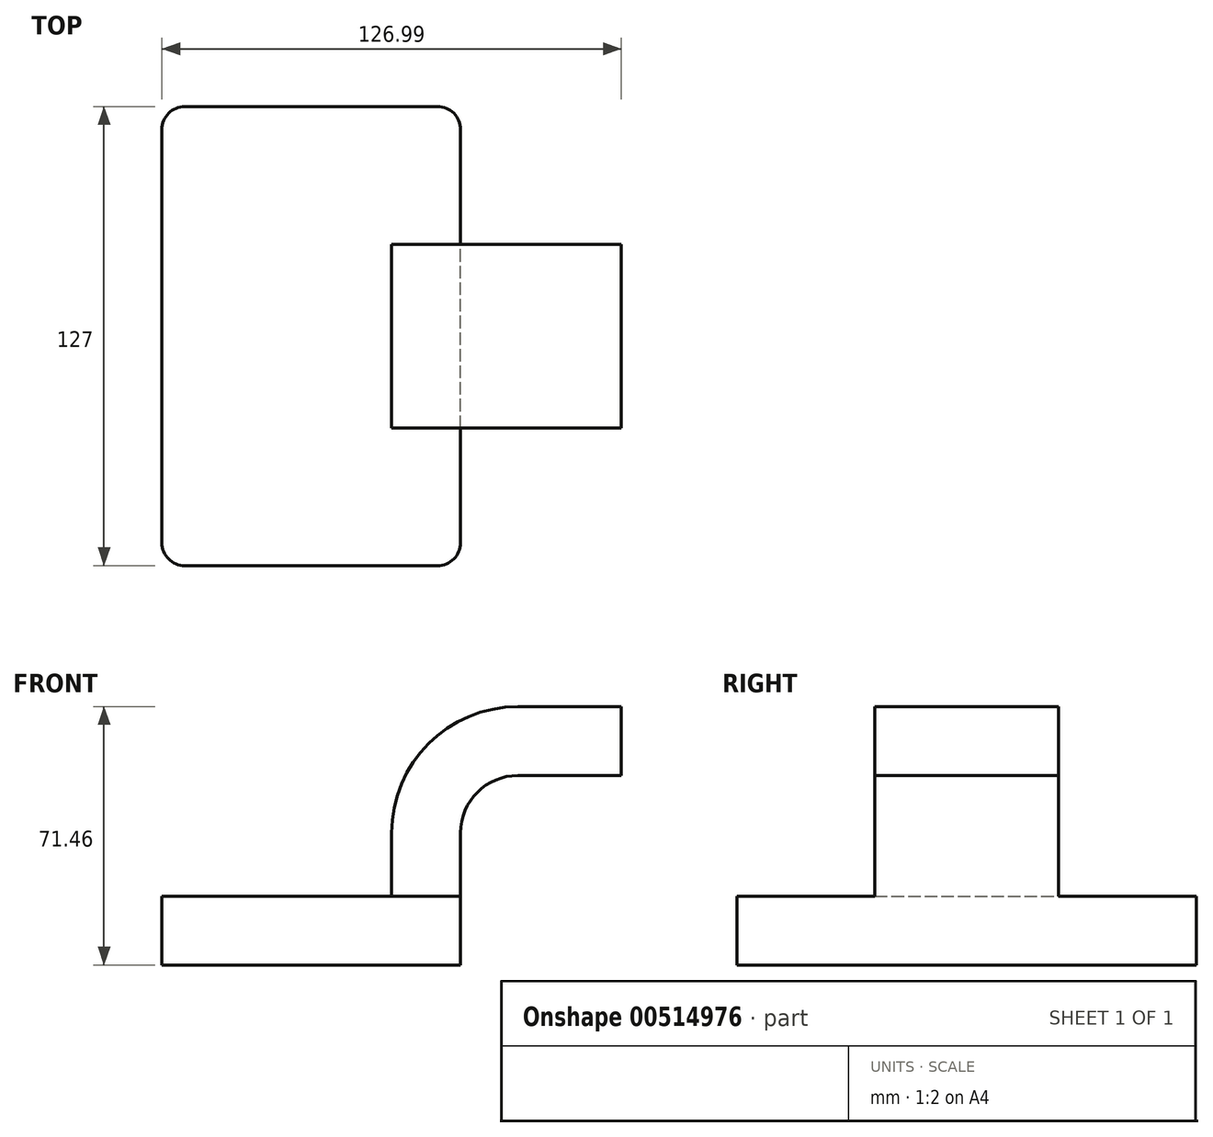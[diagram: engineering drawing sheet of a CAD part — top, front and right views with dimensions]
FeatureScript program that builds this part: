
annotation { "Feature Type Name" : "Feature", "Feature Type Description" : "" }
export const myFeature = defineFeature(function(context is Context, id is Id, definition is map)
    precondition{}
    {
        {
            var Q0;
            Q0=qCreatedBy(makeId("Front.planeOp"),FACE);
            var sketch = newSketch(context, id + "F0", { "sketchPlane" : qUnion([Q0])});
            skLineSegment(sketch, "E0.bottom", {"start": v(41.27, 9.53) * mm, "end": v(-41.28, 9.53) * mm});
            skLineSegment(sketch, "E0.top", {"start": v(41.28, -9.52) * mm, "end": v(-41.27, -9.53) * mm});
            skLineSegment(sketch, "E0.left", {"start": v(41.28, 9.53) * mm, "end": v(41.28, -9.52) * mm});
            skLineSegment(sketch, "E0.right", {"start": v(-41.28, 9.53) * mm, "end": v(-41.27, -9.53) * mm});
            skPoint(sketch, "E0.middle", {"position": v(0, 0) * mm});
            skLineSegment(sketch, "E1.bottom", {"start": v(111.13, 38.1) * mm, "end": v(60.33, 38.1) * mm});
            skLineSegment(sketch, "E1.top", {"start": v(111.13, 66.68) * mm, "end": v(60.33, 66.68) * mm});
            skLineSegment(sketch, "E1.left", {"start": v(111.13, 38.1) * mm, "end": v(111.13, 66.68) * mm});
            skLineSegment(sketch, "E1.right", {"start": v(60.33, 38.1) * mm, "end": v(60.33, 66.68) * mm});
            skPoint(sketch, "E1.middle", {"position": v(85.73, 52.39) * mm});
            skLineSegment(sketch, "E2", {"start": v(41.27, 9.53) * mm, "end": v(41.27, 27) * mm});
            skArc(sketch, "E3", {"start": v(41.28, 27) * mm, "mid": v(45.92, 38.23) * mm, "end": v(57.15, 42.88) * mm});
            skLineSegment(sketch, "E4", {"start": v(57.15, 42.88) * mm, "end": v(85.73, 42.88) * mm});
            skArc(sketch, "E5.0", {"start": v(22.23, 27) * mm, "mid": v(32.45, 51.7) * mm, "end": v(57.15, 61.93) * mm});
            skLineSegment(sketch, "E6", {"start": v(85.73, 42.88) * mm, "end": v(85.73, 61.93) * mm});
            skLineSegment(sketch, "E7", {"start": v(57.15, 61.93) * mm, "end": v(85.73, 61.93) * mm});
            skLineSegment(sketch, "E8", {"start": v(22.23, 27) * mm, "end": v(22.23, 9.53) * mm});
            skFitSpline(sketch, "E9", {"points": [v(-41.28, 9.53) * mm, v(57.15, 61.93) * mm], "startDerivative": vector(-16.87, 98.83) * mm, "endDerivative": vector(148.65, -3.4) * mm});
            skSolve(sketch);
        }
        {
            var Q0;
            Q0=makeQuery(id+"F0.imprint","IMPRINT",FACE,{"disambiguationData":[TD([[makeQuery(id+"F0.imprint","IMPRINT",EDGE,{"derivedFrom":sQuery(id+"F0.wireOp",EDGE,"E0.top")}),-1.0]])]});
            extrude(context, id + "F1", {"entities" : qUnion([Q0]), "endBound" : BoundingType.SYMMETRIC, "depth" : 127 * mm});
        }
        {
            var Q0;
            {var subQ1=sQuery(id+"F0.wireOp",EDGE,"E2");Q0=makeQuery(id+"F0.imprint","IMPRINT",FACE,{"disambiguationData":[TD([[makeQuery(id+"F0.imprint","IMPRINT",EDGE,{"derivedFrom":subQ1}),1.0]])]});}
            var Q1;
            {var subQ5=sQuery(id+"F0.wireOp",EDGE,"E6");Q1=makeQuery(id+"F0.imprint","IMPRINT",FACE,{"disambiguationData":[TD([[makeQuery(id+"F0.imprint","IMPRINT",EDGE,{"derivedFrom":subQ5}),1.0]])]});}
            extrude(context, id + "F2", {"entities" : qUnion([Q0, Q1]), "operationType" : NewBodyOperationType.ADD, "endBound" : BoundingType.SYMMETRIC, "depth" : 50.8 * mm});
        }
        {
            var Q0;
            Q0=makeQuery(id+"F0.imprint","IMPRINT",FACE,{"disambiguationData":[TD([[makeQuery(id+"F0.imprint","IMPRINT",EDGE,{"derivedFrom":sQuery(id+"F0.wireOp",EDGE,"E5.0")}),1.0]])]});
            extrude(context, id + "F3", {"entities" : qUnion([Q0]), "operationType" : NewBodyOperationType.ADD, "endBound" : BoundingType.SYMMETRIC, "depth" : 15.88 * mm});
        }
        {
            var Q0;
            Q0=makeQuery(id+"F1.opExtrude","CAP_EDGE",EDGE,{"disambiguationData":[OSD([sQuery(id+"F0.wireOp",EDGE,"E0.left")])],"isStart":false});
            var Q1;
            Q1=makeQuery(id+"F1.opExtrude","CAP_EDGE",EDGE,{"disambiguationData":[OSD([sQuery(id+"F0.wireOp",EDGE,"E0.right")])],"isStart":false});
            var Q2;
            Q2=makeQuery(id+"F1.opExtrude","CAP_EDGE",EDGE,{"disambiguationData":[OSD([sQuery(id+"F0.wireOp",EDGE,"E0.left")])],"isStart":true});
            var Q3;
            Q3=makeQuery(id+"F1.opExtrude","CAP_EDGE",EDGE,{"disambiguationData":[OSD([sQuery(id+"F0.wireOp",EDGE,"E0.right")])],"isStart":true});
            fillet(context, id + "F4", {"entities" : qUnion([Q0, Q1, Q2, Q3]), "radius" : 6.35 * mm, "tangentPropagation" : true, "allowEdgeOverflow" : false});
        }
    });
